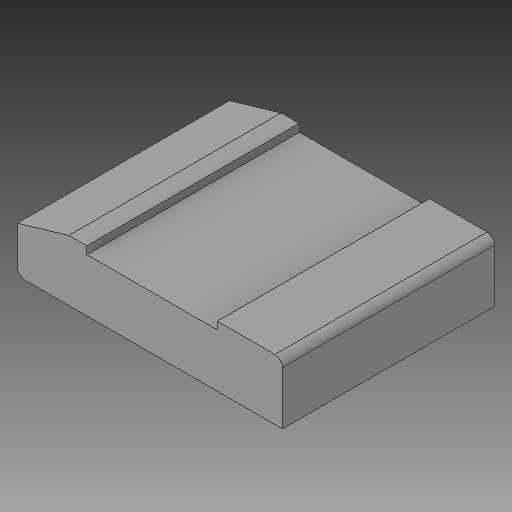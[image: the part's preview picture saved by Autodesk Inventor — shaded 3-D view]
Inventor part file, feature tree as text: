
AUTODESK INVENTOR PART (.ipt)
format: ipt  version: 2019 (Build 230136000, 136)  size: 129,024 bytes
history: native  units: in
note: dims shown in document units (in); Inventor stores cm internally (conversion verified against a paired STEP export)
features: extrude x3, sketch x3, fillet x1
ambient origin geometry x8: Origin, YZ Plane, XZ Plane, XY Plane, X Axis, Y Axis, Z Axis, Center Point
bodies: Solid1 (feature_tree)
feature tree (7):
  extrude  "Extrusion1"  Depth=3.5in
  extrude  "Extrusion2"  Depth=4.375in
  extrude  "Extrusion4"  Depth=1.075in
  fillet  "Fillet2"  Radius=0.125in
  sketch  "Sketch1"  dims[d0=4.375in d1=3.5in]
  sketch  "Sketch2"  dims[d2=1.0in d3=0.0in d4=4.375in]
  sketch  "Sketch4"  dims[d5=2.15in d6=1.075in d7=0.125in d8=0.0in d17=0.25in d18=0.3in d19=1.0in d20=0.0in d21=0.125in]
